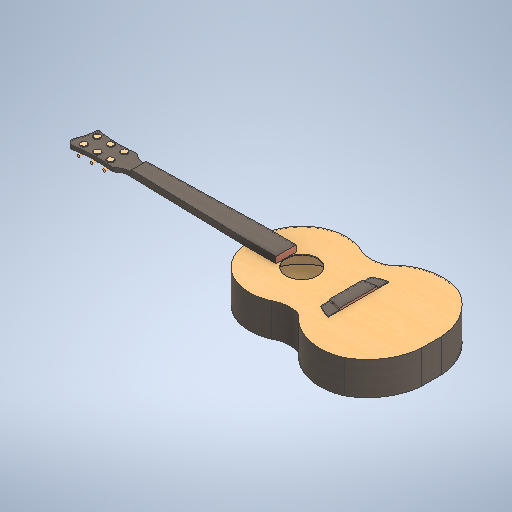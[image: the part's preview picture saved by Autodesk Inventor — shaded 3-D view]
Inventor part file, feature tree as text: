
AUTODESK INVENTOR PART (.ipt)
format: ipt  version: 2025.2 (Build 292293000, 293)  size: 904,704 bytes
history: native  units: in
note: dims shown in document units (in); Inventor stores cm internally (conversion verified against a paired STEP export)
features: extrude x11, sketch x11, plane x5, fillet x4, shell x1
ambient origin geometry x8: Origin, YZ Plane, XZ Plane, XY Plane, X Axis, Y Axis, Z Axis, Center Point
bodies: Solid1 (feature_tree)
feature tree (32):
  extrude  "Extrusion1"  Depth=0.5118in
  fillet  "Fillet3"  Radius=0.5118in
  extrude  "Extrusion3"  Depth=4.3307in
  fillet  "Fillet5"  Radius=4.3307in
  plane  "Work Plane2"
  extrude  "Extrusion4"  Depth=0.1181in
  plane  "Work Plane4"
  extrude  "Extrusion5"  Depth=13.7795in
  extrude  "Extrusion6"  Depth=0.3937in TaperAngle=0.0deg
  plane  "Work Plane3"
  extrude  "Extrusion7"  Depth=12.4016in
  extrude  "Extrusion8"  Depth=0.1575in
  fillet  "Fillet7"  Radius=0.1575in
  extrude  "Extrusion9"  Depth=2.1654in
  extrude  "Extrusion10"  Depth=0.0787in
  fillet  "Fillet8"  Radius=5.5118in
  plane  "Work Plane5"
  extrude  "Extrusion11"  Depth=2.7559in
  plane  "Work Plane6"
  extrude  "Extrusion12"  Depth=2.7559in
  shell  "Shell2"  Thickness=3.1496in
  sketch  "Sketch1"  dims[d7=1.378in d8=0.5118in d9=0.5118in]
  sketch  "Sketch3"  dims[d10=1.378in d11=4.3307in d12=4.3307in]
  sketch  "Sketch4"  dims[d13=1.5748in d14=0.1181in]
  sketch  "Sketch5"  dims[d15=0.1181in d16=13.7795in]
  sketch  "Sketch6"  dims[d17=13.7795in d18=0.3937in d19=0.0in]
  sketch  "Sketch7"  dims[d30=12.4016in d31=1.5748in]
  sketch  "Sketch8"  dims[d32=0.2953in d33=0.2953in d34=0.1575in]
  sketch  "Sketch10"  dims[d39=3.4252in d41=2.1654in]
  sketch  "Sketch11"  dims[d42=0.2756in d43=0.0in d44=0.0787in d58=5.5118in]
  sketch  "Sketch12"  dims[d59=5.5118in d63=2.7559in]
  sketch  "Sketch13"  dims[d64=3.1496in d65=2.7559in d66=3.1496in d67=4.7244in d68=4.7244in d69=3.5433in d70=0.0in d71=3.3465in d72=1.6732in d74=2.1654in d75=6.2992in d76=6.2992in d77=0.0in d78=0.0in d79=0.6051in d80=0.6051in d81=1.0579in d82=1.0579in d83=0.0in d84=0.4501in d85=0.4501in d86=3.1496in d87=0.0in d90=1.378in d91=3.5433in d92=4.7047in d94=0.2756in d95=0.2756in d96=0.2362in d97=0.0in d98=0.9055in d99=1.1811in d100=4.7244in d101=0.9055in d102=1.1811in d103=4.7244in d104=0.0787in d105=0.0in d114=0.7087in d116=0.7874in d117=0.3949in d118=0.1563in d119=0.7087in d120=0.7087in d121=1.4173in d122=1.4567in d123=0.7372in d124=0.0787in d125=0.0in d126=0.0394in d128=4.3307in d129=0.5118in d130=0.0039in d131=0.0in d132=0.3937in d133=0.0394in d134=0.3543in d135=0.3937in d136=0.0394in d137=0.3937in d138=0.0394in d139=0.9843in d140=0.9843in d141=0.3937in d142=0.0in d143=0.0394in d144=0.2756in d145=0.1969in d146=0.1969in d147=0.2756in d148=0.2756in d149=0.1969in d150=0.1969in d151=0.1969in d152=0.1969in d153=1.1811in d154=0.0in d155=0.2756in d156=0.2756in d157=0.2756in d158=0.1969in d159=0.1969in d160=0.1969in d161=0.1969in d162=0.1969in d163=0.1969in d164=1.1811in d165=0.0in d166=0.0787in d88=0.0197in d89=0.0344in]
